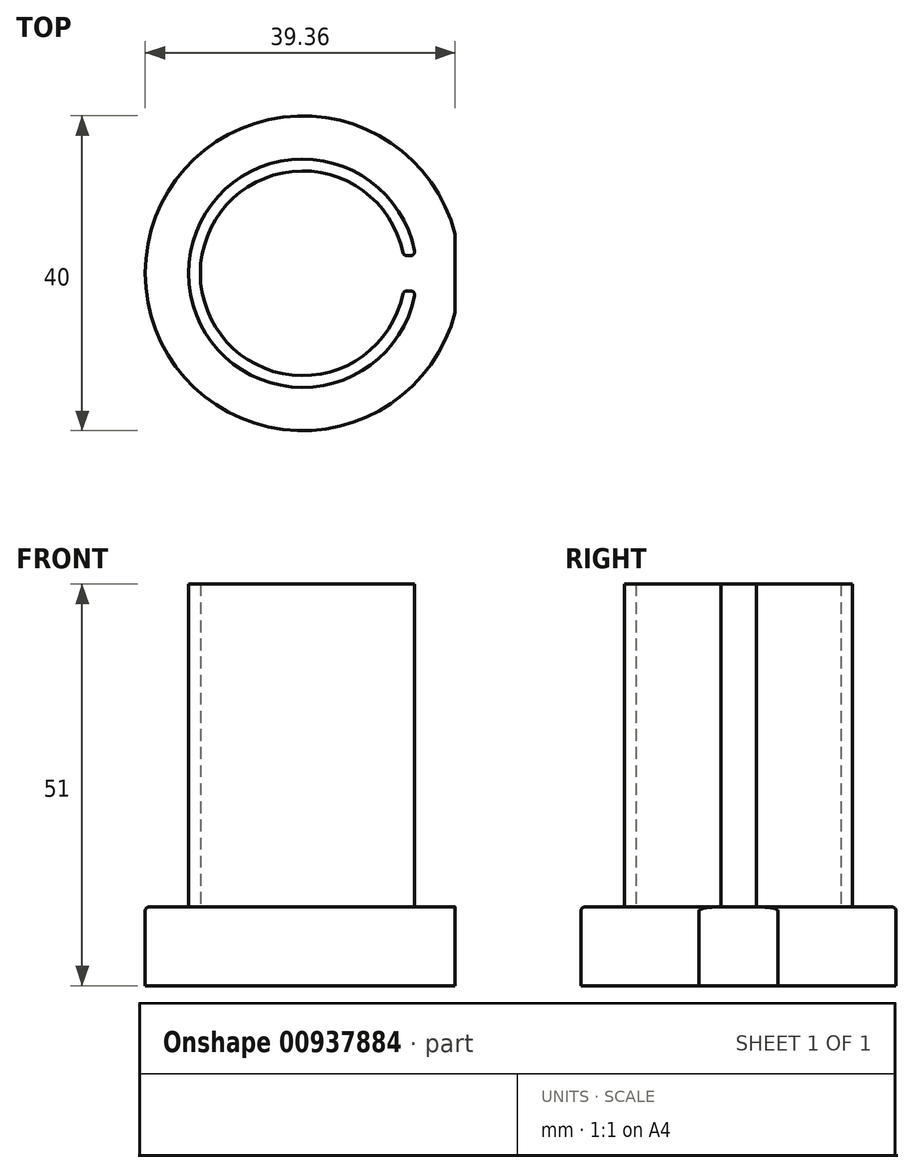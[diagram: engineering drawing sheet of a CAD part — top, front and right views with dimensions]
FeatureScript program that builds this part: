
annotation { "Feature Type Name" : "Feature", "Feature Type Description" : "" }
export const myFeature = defineFeature(function(context is Context, id is Id, definition is map)
    precondition{}
    {
        {
            var Q0;
            Q0=qCreatedBy(makeId("Top.planeOp"),FACE);
            var sketch = newSketch(context, id + "F0", { "sketchPlane" : qUnion([Q0])});
            skCircle(sketch, "E0", {"center": v(0, 0) * mm, "radius": 20 * mm});
            skLineSegment(sketch, "E1.bottom", {"start": v(19.36, -5) * mm, "end": v(-19.36, -5) * mm});
            skLineSegment(sketch, "E1.top", {"start": v(19.36, 5) * mm, "end": v(-19.36, 5) * mm});
            skLineSegment(sketch, "E1.left", {"start": v(19.36, -5) * mm, "end": v(19.36, 5) * mm});
            skLineSegment(sketch, "E1.right", {"start": v(-19.36, -5) * mm, "end": v(-19.36, 5) * mm});
            skSolve(sketch);
        }
        {
            var Q0;
            {var subQ0=sQuery(id+"F0.wireOp",EDGE,"E1.top");Q0=makeQuery(id+"F0.imprint","IMPRINT",FACE,{"disambiguationData":[TD([[makeQuery(id+"F0.imprint","IMPRINT",EDGE,{"derivedFrom":subQ0}),-1.0]])]});}
            var Q1;
            Q1=makeQuery(id+"F0.imprint","IMPRINT",FACE,{"disambiguationData":[TD([[makeQuery(id+"F0.imprint","IMPRINT",EDGE,{"derivedFrom":sQuery(id+"F0.wireOp",EDGE,"E1.bottom")}),-1.0]])]});
            var Q2;
            {var subQ0=sQuery(id+"F0.wireOp",EDGE,"E1.bottom");Q2=makeQuery(id+"F0.imprint","IMPRINT",FACE,{"disambiguationData":[TD([[makeQuery(id+"F0.imprint","IMPRINT",EDGE,{"derivedFrom":subQ0}),1.0]])]});}
            var Q3;
            {var subQ0=sQuery(id+"F0.wireOp",EDGE,"E1.right");Q3=makeQuery(id+"F0.imprint","IMPRINT",FACE,{"disambiguationData":[TD([[makeQuery(id+"F0.imprint","IMPRINT",EDGE,{"derivedFrom":subQ0}),1.0]])]});}
            extrude(context, id + "F1", {"entities" : qUnion([Q0, Q1, Q2, Q3]), "oppositeDirection" : true, "depth" : 10 * mm, "offsetDistance" : 25.4 * mm});
        }
        {
            var Q0;
            Q0=makeQuery(id+"F1.opExtrude","CAP_FACE",FACE,{"disambiguationData":[OSD([sQuery(id+"F0.wireOp",EDGE,"E0"),sQuery(id+"F0.wireOp",EDGE,"E1.left")])],"isStart":true});
            var sketch = newSketch(context, id + "F2", { "sketchPlane" : qUnion([Q0])});
            skCircle(sketch, "E2", {"center": v(0, 0) * mm, "radius": 13 * mm});
            skCircle(sketch, "E3", {"center": v(0, 0) * mm, "radius": 14.5 * mm});
            skLineSegment(sketch, "E4.bottom", {"start": v(-19.87, 2.25) * mm, "end": v(19.87, 2.25) * mm});
            skLineSegment(sketch, "E4.top", {"start": v(-19.87, -2.25) * mm, "end": v(19.87, -2.25) * mm});
            skLineSegment(sketch, "E4.left", {"start": v(-19.87, 2.25) * mm, "end": v(-19.87, -2.25) * mm});
            skLineSegment(sketch, "E4.right", {"start": v(19.87, 2.25) * mm, "end": v(19.87, -2.25) * mm});
            skSolve(sketch);
        }
        {
            var Q0;
            {var subQ0=sQuery(id+"F2.wireOp",EDGE,"E4.bottom");var subQ1=sQuery(id+"F2.wireOp",EDGE,"E2");var subQ2=makeQuery(id+"F2.imprint","INTERSECT",VERTEX,{"disambiguationData":[OD(0.0)],"derivedFrom":[subQ1,subQ0]});Q0=makeQuery(id+"F2.imprint","IMPRINT",FACE,{"disambiguationData":[TD([[makeQuery(id+"F2.imprint","IMPRINT",EDGE,{"disambiguationData":[TD([[subQ2,1.0]])],"derivedFrom":subQ1}),-1.0]])]});}
            var Q1;
            {var subQ0=sQuery(id+"F2.wireOp",EDGE,"E4.bottom");var subQ1=sQuery(id+"F2.wireOp",EDGE,"E2");var subQ2=makeQuery(id+"F2.imprint","INTERSECT",VERTEX,{"disambiguationData":[OD(0.0)],"derivedFrom":[subQ1,subQ0]});Q1=makeQuery(id+"F2.imprint","IMPRINT",FACE,{"disambiguationData":[TD([[makeQuery(id+"F2.imprint","IMPRINT",EDGE,{"disambiguationData":[TD([[subQ2,-1.0]])],"derivedFrom":subQ1}),-1.0]])]});}
            var Q2;
            {var subQ0=sQuery(id+"F2.wireOp",EDGE,"E4.top");var subQ1=sQuery(id+"F2.wireOp",EDGE,"E2");var subQ2=makeQuery(id+"F2.imprint","INTERSECT",VERTEX,{"disambiguationData":[OD(0.0)],"derivedFrom":[subQ1,subQ0]});Q2=makeQuery(id+"F2.imprint","IMPRINT",FACE,{"disambiguationData":[TD([[makeQuery(id+"F2.imprint","IMPRINT",EDGE,{"disambiguationData":[TD([[subQ2,-1.0]])],"derivedFrom":subQ1}),-1.0]])]});}
            extrude(context, id + "F3", {"entities" : qUnion([Q0, Q1, Q2]), "operationType" : NewBodyOperationType.ADD, "depth" : 41 * mm, "offsetDistance" : 25.4 * mm});
        }
        {
            var Q0;
            Q0=makeQuery(id+"F3.opExtrude","CAP_EDGE",EDGE,{"disambiguationData":[OSD([sQuery(id+"F2.wireOp",EDGE,"E3")])],"isStart":true});
            var Q1;
            Q1=makeQuery(id+"F1.opExtrude","CAP_EDGE",EDGE,{"disambiguationData":[OSD([sQuery(id+"F0.wireOp",EDGE,"E0")])],"isStart":true});
            var Q2;
            Q2=makeQuery(id+"F3.opExtrude","SWEPT_EDGE",EDGE,{"disambiguationData":[OSD([sQuery(id+"F2.wireOp",EDGE,"E2"),sQuery(id+"F2.wireOp",EDGE,"E4.bottom")])]});
            var Q3;
            Q3=makeQuery(id+"F3.opExtrude","SWEPT_EDGE",EDGE,{"disambiguationData":[OSD([sQuery(id+"F2.wireOp",EDGE,"E2"),sQuery(id+"F2.wireOp",EDGE,"E4.top")])]});
            var Q4;
            Q4=makeQuery(id+"F3.opExtrude","SWEPT_EDGE",EDGE,{"disambiguationData":[OSD([sQuery(id+"F2.wireOp",EDGE,"E3"),sQuery(id+"F2.wireOp",EDGE,"E4.bottom")])]});
            var Q5;
            Q5=makeQuery(id+"F3.opExtrude","SWEPT_EDGE",EDGE,{"disambiguationData":[OSD([sQuery(id+"F2.wireOp",EDGE,"E3"),sQuery(id+"F2.wireOp",EDGE,"E4.top")])]});
            fillet(context, id + "F4", {"entities" : qUnion([Q0, Q1, Q2, Q3, Q4, Q5]), "radius" : 0.5 * mm, "tangentPropagation" : true, "allowEdgeOverflow" : false});
        }
    });
